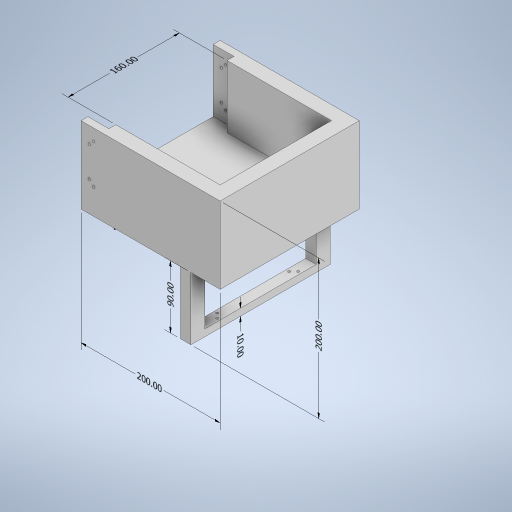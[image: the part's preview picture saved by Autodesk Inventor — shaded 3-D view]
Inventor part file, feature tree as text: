
AUTODESK INVENTOR PART (.ipt)
format: ipt  version: 2023 (Build 270158000, 158)  size: 363,008 bytes
history: native  units: mm
features: other x8, sketch x7, extrude x5, hole x2
ambient origin geometry x8: Origin, YZ Plane, XZ Plane, XY Plane, X Axis, Y Axis, Z Axis, Center Point
bodies: Body1 (feature_tree)
feature tree (22):
  other  "Sólido1"
  other  "Anotaciones"
  extrude  "Extrusión1"  Depth=200.0mm
  hole  "Agujero1"  [1 undecoded]
  extrude  "Extrusión2"  Depth=15.0mm
  extrude  "Extrusión3"  Depth=80.0mm TaperAngle=0.0deg
  extrude  "Extrusión4"  Depth=200.0mm
  extrude  "Extrusión5"  Depth=20.0mm
  hole  "Agujero2"  [1 undecoded]
  sketch  "Boceto2"  dims[d7=15.0mm d8=200.0mm]
  sketch  "Boceto3"  dims[d9=10.0mm d10=0.0mm]
  sketch  "Boceto4"  dims[d11=3.5mm d12=1.75mm d13=1.75mm d14=1.75mm d15=1.75mm d16=10.0mm d17=10.0mm d19=40.0mm]
  sketch  "Boceto5"  dims[d20=3.5mm d21=6.0mm d22=4.0mm d23=2.0mm d24=90.0deg d25=8.0mm d26=20.594885mm d27=15.0mm]
  sketch  "Boceto6"  dims[d28=20.0mm d29=80.0mm d30=0.0mm]
  sketch  "Boceto7"  dims[d31=57.0mm d32=200.0mm]
  sketch  "Boceto8"  dims[d33=110.0mm d34=0.0mm d36=20.0mm d37=20.0mm d38=20.0mm d39=90.0mm d40=0.0mm d43=30.0mm d44=0.0mm d45=3.5mm d46=1.75mm d47=1.75mm d48=1.75mm d49=1.75mm d50=10.0mm d51=10.0mm d52=15.0mm d53=10.0mm d54=10.0mm d55=15.0mm d56=3.5mm d57=6.0mm d58=4.0mm d59=2.0mm d60=90.0deg d61=8.0mm d62=20.594885mm d63=10.0mm d65=10.0mm d75=200.0mm d76=10.0mm d77=20.0mm d81=40.0mm d66=5.760865mm d67=7.72461mm d68=200.0mm d69=3.008686mm d70=2.422102mm d71=10.0mm d72=3.500509mm d73=2.402572mm d74=90.0mm d78=3.13122mm d79=6.269346mm d80=200.0mm d82=8.450127mm d83=0.968417mm d84=20.0mm d85=4.759975mm d86=4.646891mm d87=160.0mm]
  other  "Cota lineal 1"
  other  "Cota lineal 2"
  other  "Cota lineal 3"
  other  "Cota lineal 4"
  other  "Cota lineal 5"
  other  "Cota lineal 6"
note: 2 required parameter values undecoded (feature->parameter linkage not recoverable at this tier; creation-order binding heuristic only, values carry confidence <= 0.55)
